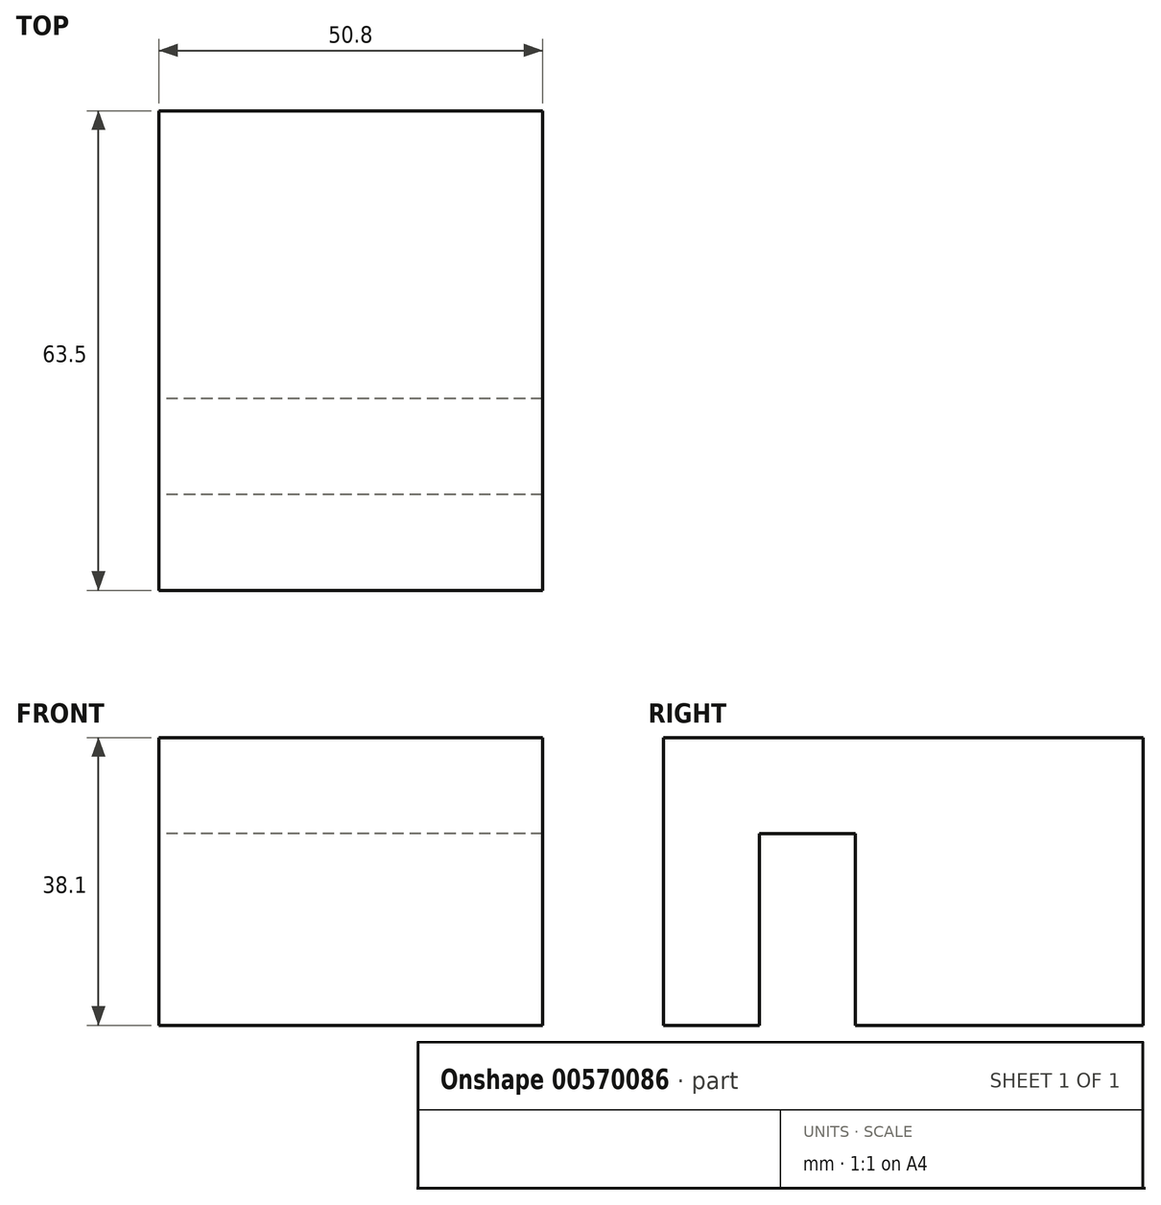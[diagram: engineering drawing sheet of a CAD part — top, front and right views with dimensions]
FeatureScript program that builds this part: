
annotation { "Feature Type Name" : "Feature", "Feature Type Description" : "" }
export const myFeature = defineFeature(function(context is Context, id is Id, definition is map)
    precondition{}
    {
        {
            var Q0;
            Q0=qCreatedBy(makeId("Right.planeOp"),FACE);
            var sketch = newSketch(context, id + "F0", { "sketchPlane" : qUnion([Q0])});
            skLineSegment(sketch, "E0", {"start": v(0, 12.7) * mm, "end": v(-63.5, 12.7) * mm});
            skLineSegment(sketch, "E1", {"start": v(-63.5, 12.7) * mm, "end": v(-63.5, -25.4) * mm});
            skLineSegment(sketch, "E2", {"start": v(-63.5, -25.4) * mm, "end": v(-50.8, -25.4) * mm});
            skLineSegment(sketch, "E3", {"start": v(-50.8, 0) * mm, "end": v(-50.8, -25.4) * mm});
            skLineSegment(sketch, "E4", {"start": v(0, 12.7) * mm, "end": v(0, -25.4) * mm});
            skLineSegment(sketch, "E5", {"start": v(0, -25.4) * mm, "end": v(-38.1, -25.4) * mm});
            skLineSegment(sketch, "E6", {"start": v(-50.8, 0) * mm, "end": v(-38.1, 0) * mm});
            skLineSegment(sketch, "E7", {"start": v(-38.1, 0) * mm, "end": v(-38.1, -25.4) * mm});
            skSolve(sketch);
        }
        {
            var Q0;
            Q0 = qSketchRegion(id + "F0", true);
            extrude(context, id + "F1", {"entities" : qUnion([Q0]), "depth" : 50.8 * mm, "offsetDistance" : 25.4 * mm});
        }
    });
